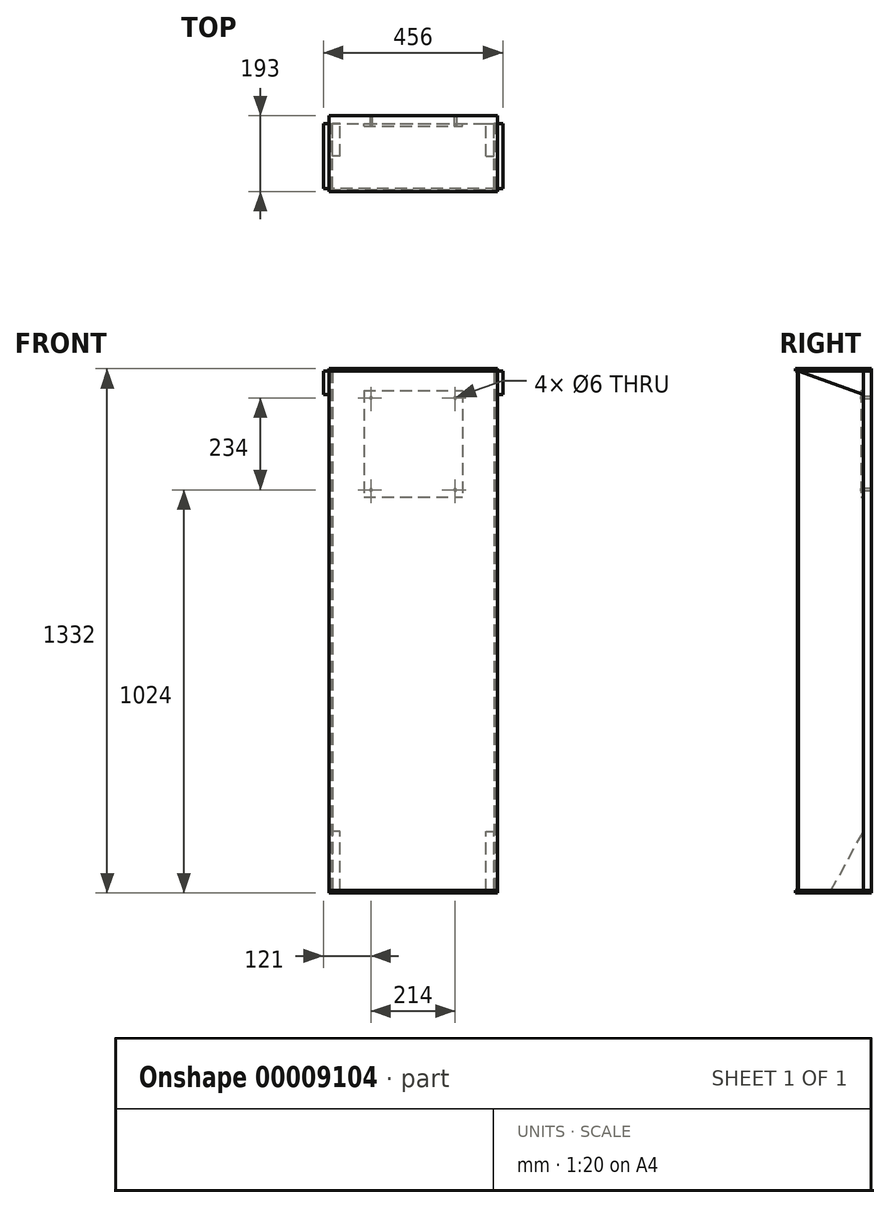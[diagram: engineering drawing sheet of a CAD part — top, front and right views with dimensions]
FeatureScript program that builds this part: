
annotation { "Feature Type Name" : "Feature", "Feature Type Description" : "" }
export const myFeature = defineFeature(function(context is Context, id is Id, definition is map)
    precondition{}
    {
        {
            var Q0;
            Q0=qCreatedBy(makeId("Front.planeOp"),FACE);
            var sketch = newSketch(context, id + "F0", { "sketchPlane" : qUnion([Q0])});
            skLineSegment(sketch, "E0.rect.bottom", {"start": v(-125, 125) * mm, "end": v(125, 125) * mm});
            skLineSegment(sketch, "E0.rect.top", {"start": v(-125, -125) * mm, "end": v(125, -125) * mm});
            skLineSegment(sketch, "E0.rect.left", {"start": v(-125, 125) * mm, "end": v(-125, -125) * mm});
            skLineSegment(sketch, "E0.rect.right", {"start": v(125, 125) * mm, "end": v(125, -125) * mm});
            skPoint(sketch, "E0.rect.middle", {"position": v(0, 0) * mm});
            skSolve(sketch);
        }
        {
            var Q0;
            Q0 = qSketchRegion(id + "F0", true);
            extrude(context, id + "F1", {"entities" : qUnion([Q0]), "depth" : 6 * mm});
        }
        {
            var Q0;
            Q0=makeQuery(id+"F1.opExtrude","CAP_FACE",FACE,{"disambiguationData":[OSD([sQuery(id+"F0.wireOp",EDGE,"E0.rect.bottom"),sQuery(id+"F0.wireOp",EDGE,"E0.rect.top"),sQuery(id+"F0.wireOp",EDGE,"E0.rect.left"),sQuery(id+"F0.wireOp",EDGE,"E0.rect.right")])],"isStart":true});
            var sketch = newSketch(context, id + "F2", { "sketchPlane" : qUnion([Q0])});
            skLineSegment(sketch, "E1.rect.bottom", {"start": v(214, 175) * mm, "end": v(-214, 175) * mm});
            skLineSegment(sketch, "E1.rect.top", {"start": v(214, -1145) * mm, "end": v(-214, -1145) * mm});
            skLineSegment(sketch, "E1.rect.left", {"start": v(214, 175) * mm, "end": v(214, -1145) * mm});
            skLineSegment(sketch, "E1.rect.right", {"start": v(-214, 175) * mm, "end": v(-214, -1145) * mm});
            skPoint(sketch, "E1.rect.middle", {"position": v(0, -485) * mm});
            skSolve(sketch);
        }
        {
            var Q0;
            Q0 = qSketchRegion(id + "F2", true);
            extrude(context, id + "F3", {"entities" : qUnion([Q0]), "depth" : 20 * mm});
        }
        {
            var Q0;
            Q0=makeQuery(id+"F3.opExtrude","SWEPT_FACE",FACE,{"disambiguationData":[OSD([sQuery(id+"F2.wireOp",EDGE,"E1.rect.bottom")])]});
            var sketch = newSketch(context, id + "F4", { "sketchPlane" : qUnion([Q0])});
            skLineSegment(sketch, "E2.bottom", {"start": v(-214, 20) * mm, "end": v(214, 20) * mm});
            skLineSegment(sketch, "E2.top", {"start": v(-214, -173) * mm, "end": v(214, -173) * mm});
            skLineSegment(sketch, "E2.left", {"start": v(-214, 20) * mm, "end": v(-214, -173) * mm});
            skLineSegment(sketch, "E2.right", {"start": v(214, 20) * mm, "end": v(214, -173) * mm});
            skSolve(sketch);
        }
        {
            var Q0;
            Q0 = qSketchRegion(id + "F4", true);
            extrude(context, id + "F5", {"entities" : qUnion([Q0]), "depth" : 6 * mm});
        }
        {
            var Q0;
            Q0=makeQuery(id+"F3.opExtrude","CAP_FACE",FACE,{"disambiguationData":[OSD([sQuery(id+"F2.wireOp",EDGE,"E1.rect.bottom"),sQuery(id+"F2.wireOp",EDGE,"E1.rect.top"),sQuery(id+"F2.wireOp",EDGE,"E1.rect.left"),sQuery(id+"F2.wireOp",EDGE,"E1.rect.right")])],"isStart":true});
            var sketch = newSketch(context, id + "F6", { "sketchPlane" : qUnion([Q0])});
            skLineSegment(sketch, "E3.bottom", {"start": v(-208, 175) * mm, "end": v(-205, 175) * mm});
            skLineSegment(sketch, "E3.top", {"start": v(-208, -1145) * mm, "end": v(-205, -1145) * mm});
            skLineSegment(sketch, "E3.left", {"start": v(-208, 175) * mm, "end": v(-208, -1145) * mm});
            skLineSegment(sketch, "E3.right", {"start": v(-205, 175) * mm, "end": v(-205, -1145) * mm});
            skSolve(sketch);
        }
        {
            var Q0;
            Q0 = qSketchRegion(id + "F6", true);
            extrude(context, id + "F7", {"entities" : qUnion([Q0]), "depth" : 165 * mm});
        }
        {
            var Q0;
            Q0=makeQuery(id+"F7.opExtrude","SWEPT_BODY",BODY,{"disambiguationData":[OSD([sQuery(id+"F6.wireOp",EDGE,"E3.bottom"),sQuery(id+"F6.wireOp",EDGE,"E3.top"),sQuery(id+"F6.wireOp",EDGE,"E3.left"),sQuery(id+"F6.wireOp",EDGE,"E3.right")])]});
            var Q1;
            Q1=qCreatedBy(makeId("Right.planeOp"),FACE);
            mirror(context, id + "F8", {"entities" : qUnion([Q0]), "mirrorPlane" : qUnion([Q1])});
        }
        {
            var Q0;
            Q0=makeQuery(id+"F5.opExtrude","CAP_FACE",FACE,{"disambiguationData":[OSD([sQuery(id+"F4.wireOp",EDGE,"E2.bottom"),sQuery(id+"F4.wireOp",EDGE,"E2.top"),sQuery(id+"F4.wireOp",EDGE,"E2.left"),sQuery(id+"F4.wireOp",EDGE,"E2.right")])],"isStart":true});
            var Q1;
            Q1=makeQuery(id+"F3.opExtrude","SWEPT_FACE",FACE,{"disambiguationData":[OSD([sQuery(id+"F2.wireOp",EDGE,"E1.rect.top")])]});
            cPlane(context, id + "F9", {"entities" : qUnion([Q0, Q1]), "cplaneType" : CPlaneType.MID_PLANE, "offset" : 150 * mm, "width" : 150 * mm, "height" : 150 * mm});
        }
        {
            var Q0;
            Q0=makeQuery(id+"F5.opExtrude","SWEPT_BODY",BODY,{"disambiguationData":[OSD([sQuery(id+"F4.wireOp",EDGE,"E2.bottom"),sQuery(id+"F4.wireOp",EDGE,"E2.top"),sQuery(id+"F4.wireOp",EDGE,"E2.left"),sQuery(id+"F4.wireOp",EDGE,"E2.right")])]});
            var Q1;
            Q1=qCreatedBy(id+"F9.planeOp",FACE);
            mirror(context, id + "F10", {"entities" : qUnion([Q0]), "mirrorPlane" : qUnion([Q1])});
        }
        {
            var Q0;
            Q0=makeQuery(id+"F5.opExtrude","CAP_FACE",FACE,{"disambiguationData":[OSD([sQuery(id+"F4.wireOp",EDGE,"E2.bottom"),sQuery(id+"F4.wireOp",EDGE,"E2.top"),sQuery(id+"F4.wireOp",EDGE,"E2.left"),sQuery(id+"F4.wireOp",EDGE,"E2.right")])],"isStart":true});
            var sketch = newSketch(context, id + "F11", { "sketchPlane" : qUnion([Q0])});
            skLineSegment(sketch, "E4.0", {"start": v(-208, 165) * mm, "end": v(-205, 165) * mm});
            skLineSegment(sketch, "E5.0", {"start": v(208, 165) * mm, "end": v(205, 165) * mm});
            skLineSegment(sketch, "E6.bottom", {"start": v(-214, 165) * mm, "end": v(214, 165) * mm});
            skLineSegment(sketch, "E6.top", {"start": v(-214, 168) * mm, "end": v(214, 168) * mm});
            skLineSegment(sketch, "E6.left", {"start": v(-214, 165) * mm, "end": v(-214, 168) * mm});
            skLineSegment(sketch, "E6.right", {"start": v(214, 165) * mm, "end": v(214, 168) * mm});
            skSolve(sketch);
        }
        {
            var Q0;
            Q0 = qSketchRegion(id + "F11", true);
            var Q1;
            Q1=makeQuery(id+"F10.opPattern","COPY",FACE,{"derivedFrom":makeQuery(id+"F5.opExtrude","CAP_FACE",FACE,{"disambiguationData":[OSD([sQuery(id+"F4.wireOp",EDGE,"E2.bottom"),sQuery(id+"F4.wireOp",EDGE,"E2.top"),sQuery(id+"F4.wireOp",EDGE,"E2.left"),sQuery(id+"F4.wireOp",EDGE,"E2.right")])],"isStart":true}),"instanceName":"1"});
            extrude(context, id + "F12", {"entities" : qUnion([Q0]), "endBound" : BoundingType.UP_TO_SURFACE, "endBoundEntityFace" : qUnion([Q1]), "depth" : 25 * mm});
        }
        {
            var Q0;
            Q0=makeQuery(id+"F7.opExtrude","SWEPT_FACE",FACE,{"disambiguationData":[OSD([sQuery(id+"F6.wireOp",EDGE,"E3.right")])]});
            var sketch = newSketch(context, id + "F13", { "sketchPlane" : qUnion([Q0])});
            skLineSegment(sketch, "E7", {"start": v(0, -995) * mm, "end": v(0, -1145) * mm});
            skLineSegment(sketch, "E8", {"start": v(0, -1145) * mm, "end": v(-82.5, -1145) * mm});
            skLineSegment(sketch, "E9", {"start": v(-82.5, -1145) * mm, "end": v(0, -995) * mm});
            skSolve(sketch);
        }
        {
            var Q0;
            Q0 = qSketchRegion(id + "F13", true);
            extrude(context, id + "F14", {"entities" : qUnion([Q0]), "depth" : 20 * mm});
        }
        {
            var Q0;
            Q0=makeQuery(id+"F14.opExtrude","SWEPT_BODY",BODY,{"disambiguationData":[OSD([sQuery(id+"F13.wireOp",EDGE,"E7"),sQuery(id+"F13.wireOp",EDGE,"E8"),sQuery(id+"F13.wireOp",EDGE,"E9")])]});
            var Q1;
            Q1=qCreatedBy(makeId("Right.planeOp"),FACE);
            mirror(context, id + "F15", {"entities" : qUnion([Q0]), "mirrorPlane" : qUnion([Q1])});
        }
        {
            var Q0;
            Q0=makeQuery(id+"F7.opExtrude","SWEPT_FACE",FACE,{"disambiguationData":[OSD([sQuery(id+"F6.wireOp",EDGE,"E3.left")])]});
            var sketch = newSketch(context, id + "F16", { "sketchPlane" : qUnion([Q0])});
            skLineSegment(sketch, "E10", {"start": v(0, 175) * mm, "end": v(165, 175) * mm});
            skLineSegment(sketch, "E11", {"start": v(165, 175) * mm, "end": v(0, 114.94) * mm});
            skLineSegment(sketch, "E12", {"start": v(0, 114.94) * mm, "end": v(0, 175) * mm});
            skSolve(sketch);
        }
        {
            var Q0;
            Q0=makeQuery(id+"F16.imprint","IMPRINT",FACE,{"disambiguationData":[TD([[makeQuery(id+"F16.imprint","IMPRINT",EDGE,{"derivedFrom":sQuery(id+"F16.wireOp",EDGE,"E10")}),1.0]])]});
            extrude(context, id + "F17", {"entities" : qUnion([Q0]), "depth" : 20 * mm});
        }
        {
            var Q0;
            Q0=makeQuery(id+"F17.opExtrude","SWEPT_BODY",BODY,{"disambiguationData":[OSD([sQuery(id+"F16.wireOp",EDGE,"E10"),sQuery(id+"F16.wireOp",EDGE,"E11"),sQuery(id+"F16.wireOp",EDGE,"E12")])]});
            var Q1;
            Q1=qCreatedBy(makeId("Right.planeOp"),FACE);
            mirror(context, id + "F18", {"entities" : qUnion([Q0]), "mirrorPlane" : qUnion([Q1])});
        }
        {
            var Q0;
            Q0=makeQuery(id+"F1.opExtrude","SWEPT_FACE",FACE,{"disambiguationData":[OSD([sQuery(id+"F0.wireOp",EDGE,"E0.rect.top")])]});
            var sketch = newSketch(context, id + "F19", { "sketchPlane" : qUnion([Q0])});
            skLineSegment(sketch, "E13.0.0", {"start": v(-125, 0) * mm, "end": v(125, 0) * mm});
            skLineSegment(sketch, "E13.0.1", {"start": v(125, 0) * mm, "end": v(125, 6) * mm});
            skLineSegment(sketch, "E13.0.2", {"start": v(125, 6) * mm, "end": v(-125, 6) * mm});
            skLineSegment(sketch, "E13.0.3", {"start": v(-125, 6) * mm, "end": v(-125, 0) * mm});
            skSolve(sketch);
        }
        {
            var Q0;
            Q0 = qSketchRegion(id + "F19", true);
            extrude(context, id + "F20", {"entities" : qUnion([Q0]), "operationType" : NewBodyOperationType.ADD, "depth" : 20 * mm});
        }
        {
            var Q0;
            Q0=makeQuery(id+"F20.boolean.opBoolean","MERGE",FACE,{"derivedFrom":[makeQuery(id+"F1.opExtrude","CAP_FACE",FACE,{"disambiguationData":[OSD([sQuery(id+"F0.wireOp",EDGE,"E0.rect.bottom"),sQuery(id+"F0.wireOp",EDGE,"E0.rect.top"),sQuery(id+"F0.wireOp",EDGE,"E0.rect.left"),sQuery(id+"F0.wireOp",EDGE,"E0.rect.right")])],"isStart":false}),makeQuery(id+"F20.opExtrude","SWEPT_FACE",FACE,{"disambiguationData":[OSD([sQuery(id+"F19.wireOp",EDGE,"E13.0.2")])]})]});
            var sketch = newSketch(context, id + "F21", { "sketchPlane" : qUnion([Q0])});
            skCircle(sketch, "E14", {"center": v(-107, 107) * mm, "radius": 3 * mm});
            skCircle(sketch, "E15", {"center": v(-107, -127) * mm, "radius": 3 * mm});
            skCircle(sketch, "E16.MirrorC", {"center": v(107, 107) * mm, "radius": 3 * mm});
            skCircle(sketch, "E17.MirrorC", {"center": v(107, -127) * mm, "radius": 3 * mm});
            skSolve(sketch);
        }
        {
            var Q0;
            Q0 = qSketchRegion(id + "F21", true);
            var Q1;
            Q1=qCreatedBy(makeId("Front.planeOp"),FACE);
            extrude(context, id + "F22", {"entities" : qUnion([Q0]), "operationType" : NewBodyOperationType.REMOVE, "endBound" : BoundingType.THROUGH_ALL, "oppositeDirection" : true, "endBoundEntityFace" : qUnion([Q1]), "depth" : 25 * mm});
        }
    });
